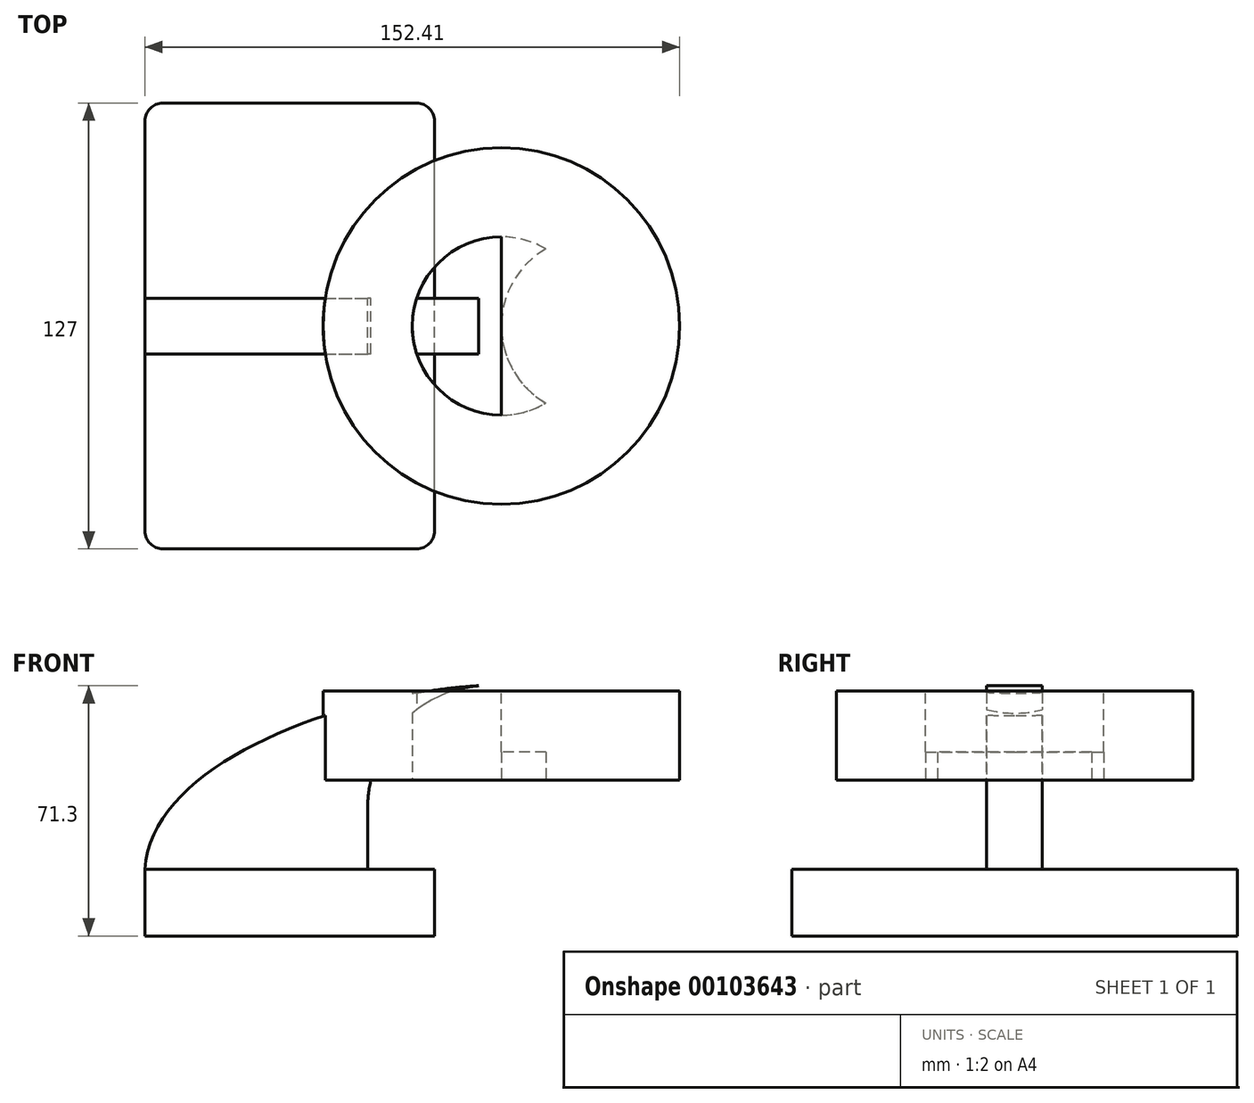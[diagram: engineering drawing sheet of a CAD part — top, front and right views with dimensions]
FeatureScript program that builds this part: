
annotation { "Feature Type Name" : "Feature", "Feature Type Description" : "" }
export const myFeature = defineFeature(function(context is Context, id is Id, definition is map)
    precondition{}
    {
        {
            var Q0;
            Q0=qCreatedBy(makeId("Front.planeOp"),FACE);
            var sketch = newSketch(context, id + "F0", { "sketchPlane" : qUnion([Q0])});
            skLineSegment(sketch, "E0.rect.bottom", {"start": v(-41.28, 9.52) * mm, "end": v(41.28, 9.52) * mm});
            skLineSegment(sketch, "E0.rect.top", {"start": v(-41.28, -9.52) * mm, "end": v(41.28, -9.52) * mm});
            skLineSegment(sketch, "E0.rect.left", {"start": v(-41.28, 9.52) * mm, "end": v(-41.28, -9.52) * mm});
            skLineSegment(sketch, "E0.rect.right", {"start": v(41.28, 9.52) * mm, "end": v(41.28, -9.52) * mm});
            skPoint(sketch, "E0.rect.middle", {"position": v(0, 0) * mm});
            skLineSegment(sketch, "E1", {"start": v(41.27, 9.52) * mm, "end": v(41.27, 27) * mm});
            skArc(sketch, "E2", {"start": v(41.28, 27) * mm, "mid": v(45.92, 38.23) * mm, "end": v(57.15, 42.88) * mm});
            skLineSegment(sketch, "E3", {"start": v(57.15, 42.88) * mm, "end": v(85.72, 42.88) * mm});
            skLineSegment(sketch, "E4.rect.bottom", {"start": v(60.32, 34.93) * mm, "end": v(111.12, 34.93) * mm});
            skLineSegment(sketch, "E4.rect.top", {"start": v(60.32, 60.33) * mm, "end": v(111.12, 60.33) * mm});
            skLineSegment(sketch, "E4.rect.left", {"start": v(60.32, 34.92) * mm, "end": v(60.32, 60.33) * mm});
            skLineSegment(sketch, "E4.rect.right", {"start": v(111.12, 34.93) * mm, "end": v(111.12, 60.33) * mm});
            skPoint(sketch, "E4.rect.middle", {"position": v(85.72, 47.63) * mm});
            skLineSegment(sketch, "E5.0", {"start": v(57.15, 61.93) * mm, "end": v(111.12, 61.93) * mm});
            skArc(sketch, "E5.1", {"start": v(22.23, 27) * mm, "mid": v(32.45, 51.7) * mm, "end": v(57.15, 61.93) * mm});
            skLineSegment(sketch, "E5.2", {"start": v(22.22, 6.35) * mm, "end": v(22.22, 27) * mm});
            skLineSegment(sketch, "E6", {"start": v(85.72, 34.93) * mm, "end": v(85.72, 60.33) * mm});
            skFitSpline(sketch, "E7", {"points": [v(-41.28, 9.53) * mm, v(57.15, 61.93) * mm], "startDerivative": vector(5.2, 92.34) * mm, "endDerivative": vector(120.92, 4.22) * mm});
            skSolve(sketch);
        }
        {
            var Q0;
            Q0=makeQuery(id+"F0.imprint","IMPRINT",FACE,{"disambiguationData":[TD([[makeQuery(id+"F0.imprint","IMPRINT",EDGE,{"derivedFrom":sQuery(id+"F0.wireOp",EDGE,"E0.rect.top")}),1.0]])]});
            extrude(context, id + "F1", {"entities" : qUnion([Q0]), "endBound" : BoundingType.SYMMETRIC, "depth" : 127 * mm});
        }
        {
            var Q0;
            {var subQ9=sQuery(id+"F0.wireOp",EDGE,"E1");Q0=makeQuery(id+"F0.imprint","IMPRINT",FACE,{"disambiguationData":[TD([[makeQuery(id+"F0.imprint","IMPRINT",EDGE,{"derivedFrom":subQ9}),1.0]])]});}
            var Q1;
            {var subQ0=sQuery(id+"F0.wireOp",EDGE,"E6");var subQ1=sQuery(id+"F0.wireOp",EDGE,"E3");var subQ2=makeQuery(id+"F0.imprint","INTERSECT",VERTEX,{"derivedFrom":[subQ1,subQ0]});Q1=makeQuery(id+"F0.imprint","IMPRINT",FACE,{"disambiguationData":[TD([[makeQuery(id+"F0.imprint","IMPRINT",EDGE,{"disambiguationData":[TD([[subQ2,1.0]])],"derivedFrom":subQ1}),1.0]])]});}
            extrude(context, id + "F2", {"entities" : qUnion([Q0, Q1]), "operationType" : NewBodyOperationType.ADD, "endBound" : BoundingType.SYMMETRIC, "depth" : 50.8 * mm});
        }
        {
            var Q0;
            {var subQ3=sQuery(id+"F0.wireOp",EDGE,"E5.2");Q0=makeQuery(id+"F0.imprint","IMPRINT",FACE,{"disambiguationData":[TD([[makeQuery(id+"F0.imprint","IMPRINT",EDGE,{"derivedFrom":subQ3}),1.0]])]});}
            extrude(context, id + "F3", {"entities" : qUnion([Q0]), "operationType" : NewBodyOperationType.ADD, "endBound" : BoundingType.SYMMETRIC, "depth" : 15.88 * mm});
        }
        {
            var Q0;
            {var subQ5=sQuery(id+"F0.wireOp",EDGE,"E4.rect.right");Q0=makeQuery(id+"F0.imprint","IMPRINT",FACE,{"disambiguationData":[TD([[makeQuery(id+"F0.imprint","IMPRINT",EDGE,{"derivedFrom":subQ5}),1.0]])]});}
            var Q1;
            Q1=sQuery(id+"F0.wireOp",EDGE,"E4.rect.left");
            revolve(context, id + "F4", {"operationType" : NewBodyOperationType.ADD, "entities" : qUnion([Q0]), "axis" : qUnion([Q1]), "revolveType" : RevolveType.FULL});
        }
        {
            var Q0;
            {var subQ5=sQuery(id+"F0.wireOp",EDGE,"E4.rect.right");Q0=makeQuery(id+"F0.imprint","IMPRINT",FACE,{"disambiguationData":[TD([[makeQuery(id+"F0.imprint","IMPRINT",EDGE,{"derivedFrom":subQ5}),1.0]])]});}
            var Q1;
            Q1=sQuery(id+"F0.wireOp",EDGE,"E6");
            revolve(context, id + "F5", {"operationType" : NewBodyOperationType.ADD, "entities" : qUnion([Q0]), "axis" : qUnion([Q1]), "revolveType" : RevolveType.FULL});
        }
        {
            var Q0;
            Q0=makeQuery(id+"F1.opExtrude","CAP_EDGE",EDGE,{"disambiguationData":[OSD([sQuery(id+"F0.wireOp",EDGE,"E0.rect.right")])],"isStart":false});
            var Q1;
            Q1=makeQuery(id+"F1.opExtrude","CAP_EDGE",EDGE,{"disambiguationData":[OSD([sQuery(id+"F0.wireOp",EDGE,"E0.rect.left")])],"isStart":false});
            var Q2;
            Q2=makeQuery(id+"F1.opExtrude","CAP_EDGE",EDGE,{"disambiguationData":[OSD([sQuery(id+"F0.wireOp",EDGE,"E0.rect.right")])],"isStart":true});
            var Q3;
            Q3=makeQuery(id+"F1.opExtrude","CAP_EDGE",EDGE,{"disambiguationData":[OSD([sQuery(id+"F0.wireOp",EDGE,"E0.rect.left")])],"isStart":true});
            fillet(context, id + "F6", {"entities" : qUnion([Q0, Q1, Q2, Q3]), "radius" : 5.08 * mm, "tangentPropagation" : true, "allowEdgeOverflow" : false});
        }
    });
